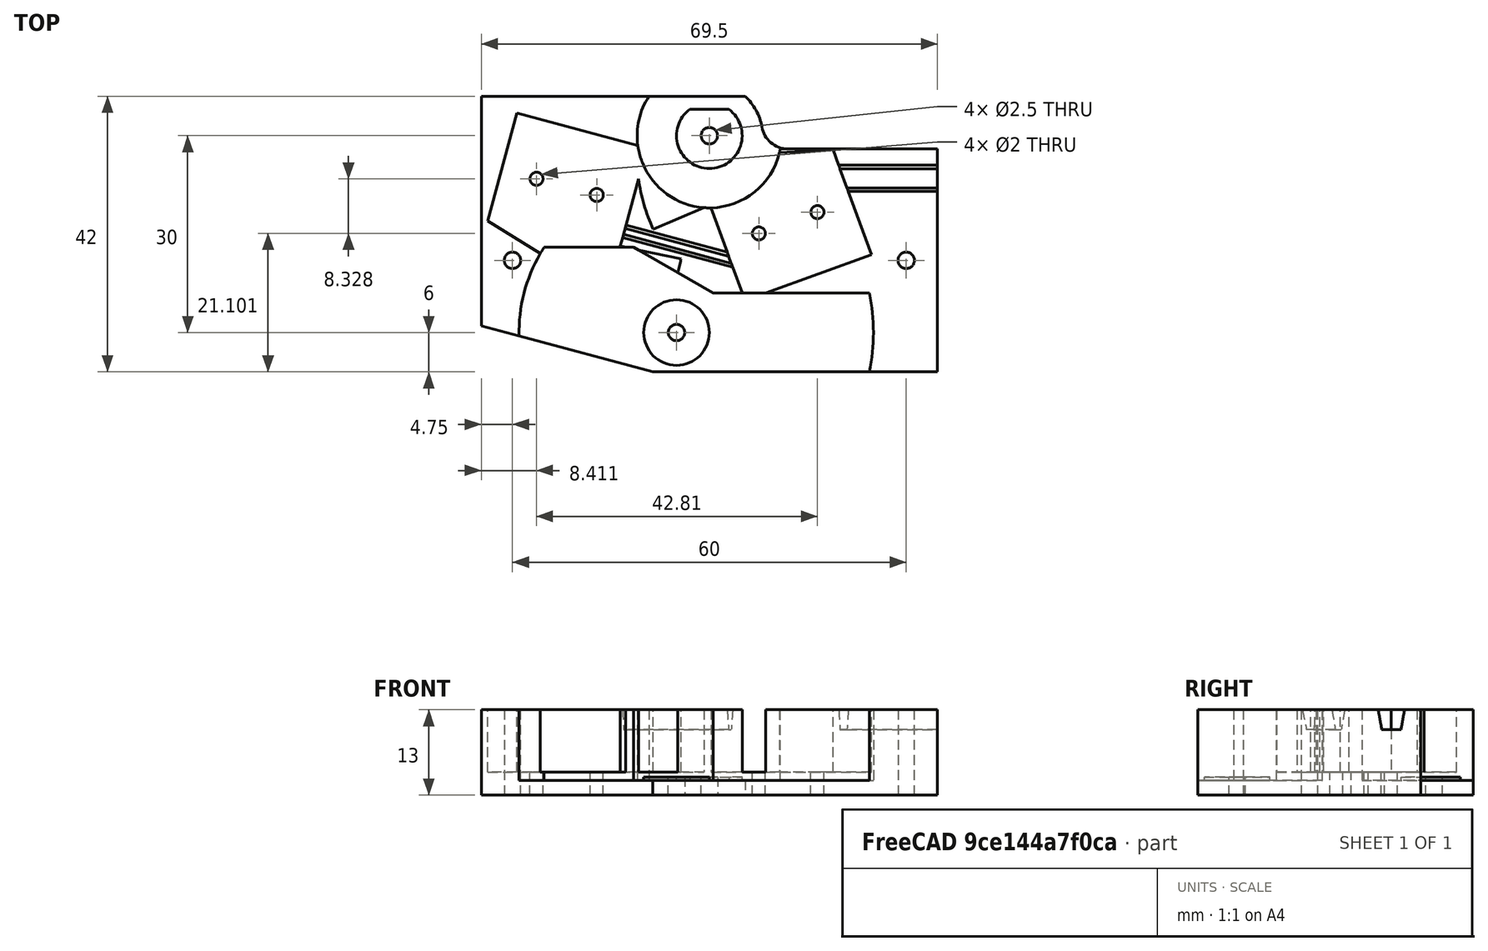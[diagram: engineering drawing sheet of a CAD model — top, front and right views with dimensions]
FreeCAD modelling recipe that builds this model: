
FCSTD DOCUMENT  (FreeCAD 1.0R39109 (Git))
Label: TriggerPlate.stl
License: All rights reserved
LicenseURL: http://en.wikipedia.org/wiki/All_rights_reserved
objects: Sketcher::SketchObject×11, PartDesign::Pocket×10, PartDesign::SubShapeBinder×4, PartDesign::Pad×3, PartDesign::Body×1, App::Part×1
note: 66 computed .brp shape members not serialized (recipe doc carries the construction recipe); baked Part::Feature solids carry a one-line shape summary decoded from their .brp

FEATURE [Sketcher::SketchObject] Sketch
  ArcFitTolerance = 1e-06
  AttachmentOffset = pos=(0,0,-6.75) rot=(0,0,1;0rad)
  AttachmentSupport = -> [XY_Plane003]
  FullyConstrained = true
  MakeInternals = false
  MapMode = 5
  Placement = pos=(0,0,-6.75) rot=(0,0,1;0rad)
  sketch-geometry (7):
    g0: LineSegment StartX=0.25 StartY=-35 StartZ=0 EndX=26.3744 EndY=-42 EndZ=0
    g1: Circle CenterX=5 CenterY=-25 CenterZ=0 NormalX=0 NormalY=0 NormalZ=1 AngleXU=0 Radius=1.25
    g2: Circle CenterX=65 CenterY=-25 CenterZ=0 NormalX=0 NormalY=0 NormalZ=1 AngleXU=0 Radius=1.25
    g3: LineSegment StartX=26.3744 StartY=-42 StartZ=0 EndX=69.75 EndY=-42 EndZ=0
    g4: LineSegment StartX=69.75 StartY=0 StartZ=0 EndX=69.75 EndY=-42 EndZ=0
    g5: LineSegment StartX=0.25 StartY=-35 StartZ=0 EndX=0.25 EndY=0 EndZ=0
    g6: LineSegment StartX=69.75 StartY=0 StartZ=0 EndX=0.25 EndY=0 EndZ=0
  constraints (21):
    c: DistanceY(g0,g-1) = 35
    c: Diameter(g1) = 2.5
    c: DistanceX(g-1,g1) = 5
    c: DistanceY(g1,g-1) = 25
    c: Equal(g2,g1)
    c: DistanceX(g1,g2) = 60
    c: Horizontal(g1,g2)
    c: Coincident(g3,g0)
    c: Horizontal(g3)
    c: Coincident(g4,g3)
    c: Vertical(g4)
    c: Distance(g0,g-2) = 0.25
    c: Coincident(g5,g0)
    c: Coincident(g6,g4)
    c: Coincident(g6,g5)
    c: Vertical(g5)
    c: Angle(g0,g5) = 1.8326
    c: DistanceX(g6,g6) = 69.5
    c: Horizontal(g6)
    c: DistanceY(g3,g-1) = 42
    c: PointOnObject(g4,g-1)
FEATURE [PartDesign::Pad] Pad
  Direction = (0,0,1)
  Length = 13
  Length2 = 10
  Profile = -> Sketch
  ReferenceAxis = -> Sketch [N_Axis]
  Refine = true
  Suppressed = false
  Type = 0
FEATURE [Sketcher::SketchObject] Sketch001
  ArcFitTolerance = 1e-06
  AttachmentOffset = pos=(0,0,-4.5) rot=(0,0,1;0rad)
  AttachmentSupport = -> [XY_Plane003]
  FullyConstrained = true
  MakeInternals = false
  MapMode = 5
  Placement = pos=(0,0,-4.5) rot=(0,0,1;0rad)
  sketch-geometry (6):
    g0: ArcOfCircle CenterX=30 CenterY=-36 CenterZ=0 NormalX=0 NormalY=0 NormalZ=1 AngleXU=0 Radius=24 StartAngle=2.56917 EndAngle=4.71239
    g1: ArcOfCircle CenterX=30 CenterY=-36 CenterZ=0 NormalX=0 NormalY=0 NormalZ=1 AngleXU=0 Radius=30 StartAngle=4.71239 EndAngle=6.48454
    g2: LineSegment StartX=30 StartY=-60 StartZ=0 EndX=30 EndY=-66 EndZ=0
    g3: LineSegment StartX=35.6077 StartY=-30 StartZ=0 EndX=59.3939 EndY=-30 EndZ=0
    g4: LineSegment StartX=35.6077 StartY=-30 StartZ=0 EndX=23.4833 EndY=-23 EndZ=0
    g5: LineSegment StartX=23.4833 StartY=-23 StartZ=0 EndX=9.82576 EndY=-23 EndZ=0
  constraints (19):
    c: Coincident(g1,g0)
    c: Coincident(g2,g0)
    c: Coincident(g2,g1)
    c: Coincident(g3,g1)
    c: Horizontal(g3)
    c: Radius(g1) = 30
    c: Radius(g0) = 24
    c: DistanceX(g-1,g0) = 30
    c: DistanceY(g0,g-1) = 36
    c: DistanceY(g0,g1) = 6
    c: Vertical(g2)
    c: Vertical(g0,g0)
    c: Coincident(g4,g3)
    c: Coincident(g5,g4)
    c: Coincident(g5,g0)
    c: Horizontal(g5)
    c: Distance(g0,g4) = 8
    c: Angle(g4,g3) = 0.523599
    c: DistanceY(g0,g0) = 13
FEATURE [PartDesign::Pocket] Pocket  label="TriggerCutout"
  BaseFeature = -> Pad
  Direction = (0,0,-1)
  Length = 5
  Length2 = 5
  Profile = -> Sketch001
  ReferenceAxis = -> Sketch001 [N_Axis]
  Refine = true
  Reversed = true
  Suppressed = false
  Type = 1
FEATURE [Sketcher::SketchObject] Sketch002
  ArcFitTolerance = 1e-06
  AttachmentOffset = pos=(0,0,-4) rot=(0,0,1;0rad)
  AttachmentSupport = -> [XY_Plane003]
  FullyConstrained = true
  MakeInternals = false
  MapMode = 5
  Placement = pos=(0,0,-4) rot=(0,0,1;0rad)
  sketch-geometry (1):
    g0: Circle CenterX=30 CenterY=-36 CenterZ=0 NormalX=0 NormalY=0 NormalZ=1 AngleXU=0 Radius=5
  constraints (3):
    c: DistanceX(g-1,g0) = 30
    c: DistanceY(g0,g-1) = 36
    c: Diameter(g0) = 10
FEATURE [PartDesign::Pad] Pad001  label="TriggerBush"
  BaseFeature = -> Pocket
  Direction = (0,0,1)
  Length = 10
  Length2 = 10
  Profile = -> Sketch002
  ReferenceAxis = -> Sketch002 [N_Axis]
  Refine = true
  Reversed = true
  Suppressed = false
  Type = 2
FEATURE [Sketcher::SketchObject] Sketch003
  ArcFitTolerance = 1e-06
  AttachmentSupport = -> [XY_Plane003]
  FullyConstrained = true
  MakeInternals = false
  MapMode = 5
  sketch-geometry (1):
    g0: Circle CenterX=30 CenterY=-36 CenterZ=0 NormalX=0 NormalY=0 NormalZ=1 AngleXU=0 Radius=1.25
  constraints (3):
    c: DistanceX(g-1,g0) = 30
    c: DistanceY(g0,g-1) = 36
    c: Diameter(g0) = 2.5
FEATURE [PartDesign::Pocket] Pocket001  label="TriggerBoltHole"
  BaseFeature = -> Pad001
  Direction = (0,0,-1)
  Length = 5
  Length2 = 5
  Midplane = true
  Profile = -> Sketch003
  ReferenceAxis = -> Sketch003 [N_Axis]
  Refine = true
  Suppressed = false
  Type = 1
FEATURE [Sketcher::SketchObject] Sketch004
  ArcFitTolerance = 1e-06
  AttachmentOffset = pos=(0,0,-4.5) rot=(0,0,1;0rad)
  AttachmentSupport = -> [XY_Plane003]
  FullyConstrained = true
  MakeInternals = false
  MapMode = 5
  Placement = pos=(0,0,-4.5) rot=(0,0,1;0rad)
  sketch-geometry (4):
    g0: ArcOfCircle CenterX=35 CenterY=-6 CenterZ=0 NormalX=0 NormalY=0 NormalZ=1 AngleXU=0 Radius=36 StartAngle=6.2276 EndAngle=7.20457
    g1: ArcOfCircle CenterX=35 CenterY=-6 CenterZ=0 NormalX=0 NormalY=0 NormalZ=1 AngleXU=0 Radius=11 StartAngle=2.18166 EndAngle=6.10035
    g2: LineSegment StartX=28.6907 StartY=3.01067 StartZ=0 EndX=56.7698 EndY=22.6719 EndZ=0
    g3: LineSegment StartX=45.8167 StartY=-8 StartZ=0 EndX=70.9444 EndY=-8 EndZ=0
  constraints (12):
    c: Coincident(g1,g0)
    c: Coincident(g2,g0)
    c: Coincident(g3,g1)
    c: Coincident(g3,g0)
    c: Horizontal(g3)
    c: DistanceY(g0,g-1) = 6
    c: DistanceX(g-1,g0) = 35
    c: DistanceY(g0,g0) = 2
    c: Radius(g1) = 11
    c: Tangent(g2,g1) = 1.5708
    c: Angle(g-1,g2) = 0.610865
    c: Radius(g0) = 36
FEATURE [PartDesign::Pocket] Pocket002  label="LoadingLeverCutout1"
  BaseFeature = -> Pocket001
  Direction = (0,0,-1)
  Length = 5
  Length2 = 5
  Profile = -> Sketch004
  ReferenceAxis = -> Sketch004 [N_Axis]
  Refine = true
  Reversed = true
  Suppressed = false
  Type = 1
FEATURE [Sketcher::SketchObject] Sketch005
  ArcFitTolerance = 1e-06
  AttachmentSupport = -> [XY_Plane003]
  FullyConstrained = true
  MakeInternals = false
  MapMode = 5
  sketch-geometry (5):
    g0: LineSegment StartX=75 StartY=-3.6e-15 StartZ=0 EndX=40.4584 EndY=-3.6e-15 EndZ=0
    g1: LineSegment StartX=46.9451 StartY=-8 StartZ=0 EndX=75 EndY=-8 EndZ=0
    g2: LineSegment StartX=75 StartY=-8 StartZ=0 EndX=75 EndY=-3.6e-15 EndZ=0
    g3: ArcOfCircle CenterX=46.9451 CenterY=-4 CenterZ=0 NormalX=0 NormalY=0 NormalZ=1 AngleXU=0 Radius=4 StartAngle=3.30749 EndAngle=4.71239
    g4: ArcOfCircle CenterX=35 CenterY=-6 CenterZ=0 NormalX=0 NormalY=0 NormalZ=1 AngleXU=0 Radius=8.11136 StartAngle=0.165894 EndAngle=0.832629
  constraints (15):
    c: Coincident(g1,g2)
    c: Coincident(g2,g0)
    c: Horizontal(g0)
    c: Horizontal(g1)
    c: Vertical(g2)
    c: PointOnObject(g0,g-1)
    c: Tangent(g1,g3) = -1.5708
    c: Radius(g3) = 4
    c: DistanceY(g1,g-1) = 8
    c: DistanceX(g-1,g0) = 75
    c: Coincident(g4,g0)
    c: DistanceX(g-1,g3) = 43
    c: DistanceY(g4,g-1) = 6
    c: DistanceX(g-1,g4) = 35
    c: Tangent(g4,g3) = 1.5708
FEATURE [PartDesign::Pocket] Pocket003  label="LoadingLeverCutout2"
  BaseFeature = -> Pocket002
  Direction = (0,0,-1)
  Length = 5
  Length2 = 5
  Midplane = true
  Profile = -> Sketch005
  ReferenceAxis = -> Sketch005 [N_Axis]
  Refine = true
  Suppressed = false
  Type = 1
FEATURE [Sketcher::SketchObject] Sketch006  label="KW-12CutoutBase"
  ArcFitTolerance = 1e-06
  AttachmentSupport = -> [XY_Plane004]
  FullyConstrained = true
  MakeInternals = false
  MapMode = 5
  sketch-geometry (7):
    g0: LineSegment StartX=-10.25 StartY=9.5 StartZ=0 EndX=-10.25 EndY=-6 EndZ=0
    g1: LineSegment StartX=-10.25 StartY=-6 StartZ=0 EndX=10.25 EndY=-6 EndZ=0
    g2: LineSegment StartX=10.25 StartY=-6 StartZ=0 EndX=10.25 EndY=11 EndZ=0
    g3: LineSegment StartX=10.25 StartY=11 StartZ=0 EndX=-18.4391 EndY=19.7712 EndZ=0
    g4: ArcOfCircle CenterX=10.25 CenterY=11 CenterZ=0 NormalX=0 NormalY=0 NormalZ=1 AngleXU=0 Radius=30 StartAngle=2.84489 EndAngle=3.20812
    g5: LineSegment StartX=-19.6836 StartY=9.0056 StartZ=0 EndX=-10.25 EndY=9.5 EndZ=0
    g6: GeomPoint [constr] X=10.25 Y=11 Z=0
  constraints (18):
    c: Coincident(g0,g1)
    c: Coincident(g1,g2)
    c: Vertical(g0)
    c: Vertical(g2)
    c: DistanceX(g0,g6) = 20.5
    c: DistanceY(g1,g-1) = 6
    c: Symmetric(g1,g0,g-2)
    c: Coincident(g4,g6)
    c: Coincident(g4,g3)
    c: Coincident(g5,g4)
    c: Coincident(g5,g0)
    c: DistanceY(g-1,g0) = 9.5
    c: Distance(g6,g3) = 30
    c: DistanceY(g-1,g6) = 11
    c: Angle(g3,g5) = 0.349066
    c: Coincident(g2,g4)
    c: Coincident(g3,g2)
    c: Angle(g3,g-1) = 0.296706
FEATURE [PartDesign::SubShapeBinder] Binder
  BindCopyOnChange = 0
  BindMode = 0
  ClaimChildren = false
  Context = -> Part001 [Body.Binder.]
  Fuse = false
  MakeFace = true
  OffsetFill = false
  OffsetIntersection = false
  OffsetJoinType = 0
  OffsetOpenResult = false
  PartialLoad = false
  Placement = pos=(14,-11,-3.25) rot=(0,0,1;2.87979rad)
  Refine = true
  Relative = true
  Support = -> [Sketch006]
  _Version = 2
FEATURE [PartDesign::SubShapeBinder] Binder001
  BindCopyOnChange = 0
  BindMode = 0
  ClaimChildren = false
  Context = -> Part001 [Body.Binder001.]
  Fuse = false
  MakeFace = true
  OffsetFill = false
  OffsetIntersection = false
  OffsetJoinType = 0
  OffsetOpenResult = false
  PartialLoad = false
  Placement = pos=(48,-22,-3.25) rot=(0,0,1;0.349066rad)
  Refine = true
  Relative = true
  Support = -> [Sketch006]
  _Version = 2
FEATURE [Sketcher::SketchObject] Sketch007  label="KW12ScrewholeBase"
  ArcFitTolerance = 1e-06
  AttachmentSupport = -> [XY_Plane003]
  FullyConstrained = true
  MakeInternals = false
  MapMode = 5
  sketch-geometry (2):
    g0: Circle CenterX=-4.75 CenterY=2.9 CenterZ=0 NormalX=0 NormalY=0 NormalZ=1 AngleXU=0 Radius=1
    g1: Circle CenterX=4.75 CenterY=2.9 CenterZ=0 NormalX=0 NormalY=0 NormalZ=1 AngleXU=0 Radius=1
  constraints (5):
    c: Symmetric(g1,g0,g-2)
    c: DistanceY(g-1,g1) = 2.9
    c: DistanceX(g0,g1) = 9.5
    c: Equal(g1,g0)
    c: Diameter(g1) = 2
FEATURE [PartDesign::SubShapeBinder] Binder002  label="TriggerSwitchScrewHolderBinder"
  BindCopyOnChange = 0
  BindMode = 0
  ClaimChildren = false
  Context = -> Part001 [Body.Binder002.]
  Fuse = false
  MakeFace = true
  OffsetFill = false
  OffsetIntersection = false
  OffsetJoinType = 0
  OffsetOpenResult = false
  PartialLoad = false
  Placement = pos=(14,-11,0) rot=(0,0,1;2.87979rad)
  Refine = true
  Relative = true
  Support = -> [Sketch007]
  _Version = 2
FEATURE [PartDesign::SubShapeBinder] Binder003
  BindCopyOnChange = 0
  BindMode = 0
  ClaimChildren = false
  Context = -> Part001 [Body.Binder003.]
  Fuse = false
  MakeFace = true
  OffsetFill = false
  OffsetIntersection = false
  OffsetJoinType = 0
  OffsetOpenResult = false
  PartialLoad = false
  Placement = pos=(48,-22,0) rot=(0,0,1;0.349066rad)
  Refine = true
  Relative = true
  Support = -> [Sketch007]
  _Version = 2
FEATURE [Sketcher::SketchObject] Sketch008
  ArcFitTolerance = 1e-06
  AttachmentOffset = pos=(0,0,6.25) rot=(0,0,1;0rad)
  AttachmentSupport = -> [XY_Plane003]
  FullyConstrained = true
  MakeInternals = false
  MapMode = 5
  Placement = pos=(0,0,6.25) rot=(0,0,1;0rad)
  sketch-geometry (8):
    g0: LineSegment StartX=20 StartY=-19 StartZ=0 EndX=19.4824 EndY=-20.9319 EndZ=0
    g1: LineSegment StartX=19.4824 StartY=-20.9319 StartZ=0 EndX=40.7327 EndY=-26.6259 EndZ=0
    g2: LineSegment StartX=40.7327 StartY=-26.6259 StartZ=0 EndX=41.2504 EndY=-24.694 EndZ=0
    g3: LineSegment StartX=41.2504 StartY=-24.694 StartZ=0 EndX=20 EndY=-19 EndZ=0
    g4: LineSegment StartX=50 StartY=-10.5 StartZ=0 EndX=50 EndY=-14.5 EndZ=0
    g5: LineSegment StartX=50 StartY=-14.5 StartZ=0 EndX=75 EndY=-14.5 EndZ=0
    g6: LineSegment StartX=75 StartY=-14.5 StartZ=0 EndX=75 EndY=-10.5 EndZ=0
    g7: LineSegment StartX=75 StartY=-10.5 StartZ=0 EndX=50 EndY=-10.5 EndZ=0
  constraints (24):
    c: Coincident(g0,g1)
    c: Coincident(g1,g2)
    c: Coincident(g2,g3)
    c: Coincident(g3,g0)
    c: Parallel(g0,g2)
    c: Parallel(g1,g3)
    c: Distance(g0,g0) = 2
    c: Perpendicular(g0,g1)
    c: Angle(g3,g-1) = 0.261799
    c: DistanceX(g-1,g0) = 20
    c: DistanceY(g0,g-1) = 19
    c: Distance(g1,g1) = 22
    c: Coincident(g4,g5)
    c: Coincident(g5,g6)
    c: Coincident(g6,g7)
    c: Coincident(g7,g4)
    c: Vertical(g4)
    c: Vertical(g6)
    c: Horizontal(g5)
    c: Horizontal(g7)
    c: DistanceX(g-1,g6) = 75
    c: DistanceX(g7,g7) = 25
    c: DistanceY(g6,g-1) = 10.5
    c: DistanceY(g4,g4) = 4
FEATURE [Sketcher::SketchObject] Sketch009
  ArcFitTolerance = 1e-06
  AttachmentOffset = pos=(0,0,-4) rot=(0,0,1;0rad)
  AttachmentSupport = -> [XY_Plane003]
  FullyConstrained = true
  MakeInternals = false
  MapMode = 5
  Placement = pos=(0,0,-4) rot=(0,0,1;0rad)
  sketch-geometry (3):
    g0: Circle [constr] CenterX=35 CenterY=-6 CenterZ=0 NormalX=0 NormalY=0 NormalZ=1 AngleXU=0 Radius=5
    g1: ArcOfCircle CenterX=35 CenterY=-6 CenterZ=0 NormalX=0 NormalY=0 NormalZ=1 AngleXU=0 Radius=5 StartAngle=2.2143 EndAngle=7.21048
    g2: LineSegment StartX=32 StartY=-2 StartZ=0 EndX=38 EndY=-2 EndZ=0
  constraints (9):
    c: Diameter(g0) = 10
    c: DistanceY(g0,g-1) = 6
    c: DistanceX(g-1,g0) = 35
    c: Coincident(g1,g0)
    c: PointOnObject(g1,g0)
    c: Coincident(g2,g1)
    c: Coincident(g2,g1)
    c: DistanceY(g1,g-1) = 2
    c: Horizontal(g2)
FEATURE [PartDesign::Pad] Pad002  label="LoadingLeverBush"
  BaseFeature = -> Pocket003
  Direction = (0,0,1)
  Length = 10
  Length2 = 10
  Profile = -> Sketch009
  ReferenceAxis = -> Sketch009 [N_Axis]
  Refine = true
  Reversed = true
  Suppressed = false
  Type = 2
FEATURE [Sketcher::SketchObject] Sketch010
  ArcFitTolerance = 1e-06
  AttachmentSupport = -> [XY_Plane003]
  FullyConstrained = true
  MakeInternals = false
  MapMode = 5
  sketch-geometry (1):
    g0: Circle CenterX=35 CenterY=-6 CenterZ=0 NormalX=0 NormalY=0 NormalZ=1 AngleXU=0 Radius=1.25
  constraints (3):
    c: Diameter(g0) = 2.5
    c: DistanceX(g-1,g0) = 35
    c: DistanceY(g0,g-1) = 6
FEATURE [PartDesign::Pocket] Pocket009  label="LoadingLeverBoltHole"
  BaseFeature = -> Pad002
  Direction = (0,0,-1)
  Length = 5
  Length2 = 5
  Midplane = true
  Profile = -> Sketch010
  ReferenceAxis = -> Sketch010 [N_Axis]
  Refine = true
  Suppressed = false
  Type = 1
FEATURE [PartDesign::Pocket] Pocket004  label="TriggerSwitchcutout"
  BaseFeature = -> Pocket009
  Direction = (0,0,-1)
  Length = 5
  Length2 = 5
  Profile = -> Binder
  Refine = true
  Reversed = true
  Suppressed = false
  Type = 1
FEATURE [PartDesign::Pocket] Pocket005  label="LoadingSwitchCutout"
  BaseFeature = -> Pocket004
  Direction = (0,0,-1)
  Length = 5
  Length2 = 5
  Profile = -> Binder001
  Refine = true
  Reversed = true
  Suppressed = false
  Type = 1
FEATURE [PartDesign::Pocket] Pocket006  label="TriggerSwitchScrewHoles"
  BaseFeature = -> Pocket005
  Direction = (0,0,-1)
  Length = 5
  Length2 = 5
  Midplane = true
  Profile = -> Binder002
  Refine = true
  Suppressed = false
  Type = 1
FEATURE [PartDesign::Pocket] Pocket007  label="LoadingSwitchScrewHoles"
  BaseFeature = -> Pocket006
  Direction = (0,0,-1)
  Length = 5
  Length2 = 5
  Midplane = true
  Profile = -> Binder003
  Refine = true
  Suppressed = false
  Type = 1
FEATURE [PartDesign::Pocket] Pocket008  label="WireRun"
  BaseFeature = -> Pocket007
  Direction = (0,0,-1)
  Length = 3
  Length2 = 5
  Profile = -> Sketch008
  ReferenceAxis = -> Sketch008 [N_Axis]
  Refine = true
  Suppressed = false
  TaperAngle = -10
  Type = 0
FEATURE [PartDesign::Body] Body
  AllowCompound = false
  Group = -> [Sketch,Pad,Sketch001,Pocket,Sketch002,Pad001,Sketch003,Pocket001,Sketch004,Pocket002,Sketch005,Pocket003,Sketch006,Binder,Sketch009,Pad002,Sketch010,Pocket009,Pocket004,Binder001,Pocket005,Sketch007,Binder002,Pocket006,Binder003,Pocket007,Sketch008,Pocket008]
  Origin = -> Origin003
  Tip = -> Pocket008
FEATURE [App::Part] Part001  label="TriggerPlate.stl"
  Group = -> [Body]
  Origin = -> Origin004
